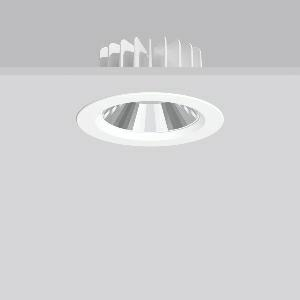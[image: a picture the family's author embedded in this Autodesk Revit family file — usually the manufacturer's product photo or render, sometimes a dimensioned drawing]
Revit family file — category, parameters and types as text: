
# Revit family: ledona_round_ip20_901795_002_76_3c7e
name_source: partatom
category: Lighting Fixtures
units: mm (PartAtom-declared; Revit-internal decimal feet)

## family parameters
Cut with Voids When Loaded = No
Host = Face
Light Source = No
Part Type = Normal
Room Calculation Point = No
Round Connector Dimension = Use Diameter
Shared = No

## types (1)
- MultiLumen 1 (1 x LED Modul 930, 1650 lm, 3000)
    Apparent Load = 12 VA
    Approval mark = CE
    CIE Flux Codes = 91 100 100 100 100
    Color Rendering = 90
    Color Temperature = 3000
    Default Elevation = 1800 mm
    Description = Series: LEDONA round
Recessed LED downlight featuring advanced technology and sophisticated design. Housing: die-cast aluminium constructed as heat sink.Bezel ring: die-cast aluminium, powder-coated. Open version. Highly polished four-segment faceted aluminium reflector with light mixing chamber. MultiLumen: Luminous flux adjustable in different steps. Best colour rendering index Ra>90. Installation without tools thanks to spring fastening system. Connected converter included in separate gearbox. With connecting cable (L 250 mm). Suitable for through wiring as standard. 
Colour: white
Diameter: 180 mm
Height: 3 mm
Cut-out diameter: 160 mm
Recess height: 89 mm
Luminaire: recess height: 89 mm
Lamp: LED
Socket: without socket
Colour temperature: 3000K
Colour rendering index (CRI): 92
System power: 12 W
Rated luminous flux: 1650 lm
Luminous efficiency: 138 lm/W
System power 2: 19 W
Rated luminous flux 2: 2550 lm
Luminous efficiency 2: 134 lm/W
System power 3: 27 W
Rated luminous flux 3: 3450 lm
Luminous efficiency 3: 128 lm/W
System power 4: 39 W
Rated luminous flux 4: 4600 lm
Luminous efficiency 4: 118 lm/W
Control gear: Converter, dimmable, DALI
Protection class: II
Type of protection: IP 20
    Height = 0 mm  [stored 0 ft]
    Lamp = 1 x LED Modul 930
    Lamp Light Flux = 1650 lm
    Lamp count = 1
    Length = 180 mm  [stored 0.590551 ft]
    Lifetime = 50000 h
    Luminous efficacy = 138 lm/W
    Manufacturer = RZB
    ModVariant = No
    Model = 901795.002.76
    Mounting Place = Ceiling
    Mounting Type = Recessed
    Number of Poles = 1
    OnlyDefault = Yes
    Power Factor = 1
    Product Name = LEDONA round IP20
    Product group = Recessed downlights
    ProductGroupID = 402
    Protection Class = Protection class II
    Protection Degree = IP 20
    RLX_Detail_Level = 1
    RLX_Emergency_Light_Flux = 0 lm
    RLX_Emergency_Type = 0
    RLX_Emergency_Type_DB = No
    RlxData = <blob elided: 37957 chars, md5=ce9c989c>
    Socket = socket
    Standby Power = 0 W
    System Light Flux = 1650 lm
    System Power = 12 W
    Type Comments = MultiLumen 1
    Type Image = 901385.002.jpg
    URL = http://relux.com
    VarID = multilumen_1
    Voltage = 230 V
    Voltage Range = 220-240 V
    Weight = 0.00 kg
    Width = 0 mm  [stored 0 ft]

note: [stored X ft] marks values corroborated as IEEE doubles in the binary element streams (Revit-internal decimal feet)

## geometry (parser evidence)
native form markers: Blend x4, Sweep x11
no freeform markers — native parametric forms only
